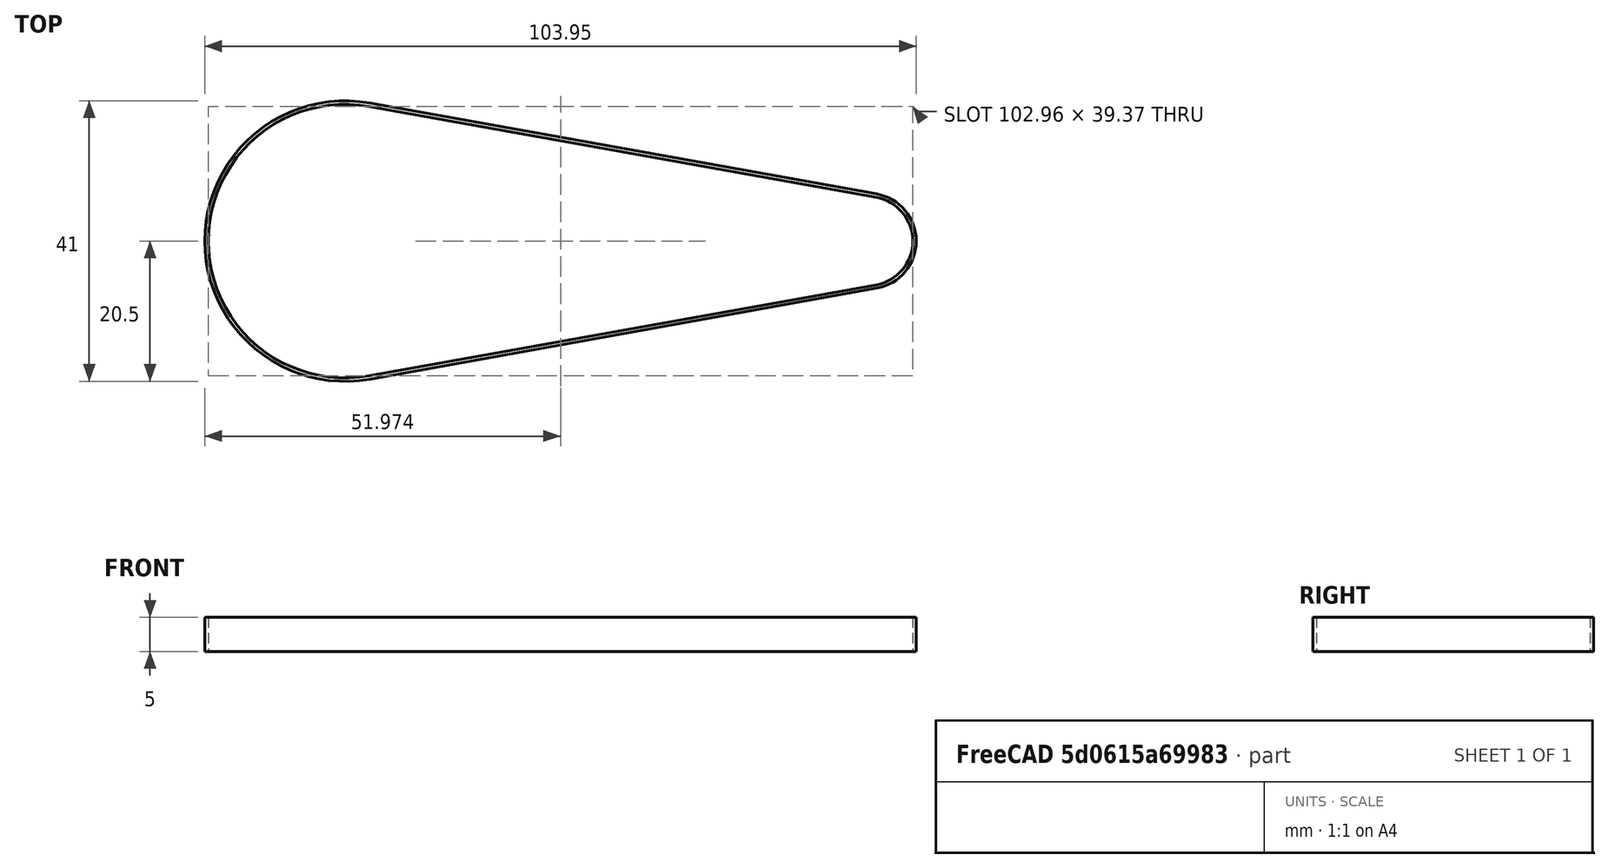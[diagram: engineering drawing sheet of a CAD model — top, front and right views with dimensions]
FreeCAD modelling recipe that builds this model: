
FCSTD DOCUMENT  (FreeCAD 0.20R29177 +426 (Git))
Label: smallerBelt
License: All rights reserved
LicenseURL: http://en.wikipedia.org/wiki/All_rights_reserved
objects: PartDesign::CoordinateSystem×2, Sketcher::SketchObject×1, PartDesign::Pad×1, PartDesign::Body×1
note: 6 computed .brp shape members not serialized (recipe doc carries the construction recipe); baked Part::Feature solids carry a one-line shape summary decoded from their .brp

FEATURE [Sketcher::SketchObject] Sketch
  FullyConstrained = false
  MapMode = 5
  Support = -> [XY_Plane]
  sketch-geometry (8):
    g0: ArcOfCircle CenterX=-48.7141 CenterY=0 CenterZ=0 NormalX=0 NormalY=0 NormalZ=1 AngleXU=0 Radius=20 StartAngle=1.3933 EndAngle=4.88989
    g1: ArcOfCircle CenterX=27.743 CenterY=0 CenterZ=0 NormalX=0 NormalY=0 NormalZ=1 AngleXU=0 Radius=6.5 StartAngle=4.88989 EndAngle=7.67648
    g2: LineSegment StartX=-45.1827 StartY=19.6858 StartZ=0 EndX=28.8907 EndY=6.39787 EndZ=0
    g3: LineSegment StartX=-45.1827 StartY=-19.6858 StartZ=0 EndX=28.8907 EndY=-6.39787 EndZ=0
    g4: ArcOfCircle CenterX=-48.7141 CenterY=0 CenterZ=0 NormalX=0 NormalY=0 NormalZ=1 AngleXU=0 Radius=20.5 StartAngle=1.3933 EndAngle=4.88989
    g5: ArcOfCircle CenterX=27.743 CenterY=0 CenterZ=0 NormalX=0 NormalY=0 NormalZ=1 AngleXU=0 Radius=7 StartAngle=4.88989 EndAngle=7.67648
    g6: LineSegment StartX=-45.0944 StartY=20.1779 StartZ=0 EndX=28.979 EndY=6.89002 EndZ=0
    g7: LineSegment StartX=-45.0944 StartY=-20.1779 StartZ=0 EndX=28.979 EndY=-6.89002 EndZ=0
  constraints (16):
    c: PointOnObject(g0,g-1)
    c: PointOnObject(g1,g-1)
    c: Diameter(g0) = 40
    c: Diameter(g1) = 13
    c: Tangent(g0,g3) = -1.5708
    c: Tangent(g0,g2) = 1.5708
    c: Tangent(g1,g2) = 1.5708
    c: Tangent(g1,g3) = -1.5708
    c: Diameter(g4) = 41
    c: Diameter(g5) = 14
    c: Tangent(g4,g7) = -1.5708
    c: Tangent(g4,g6) = 1.5708
    c: Tangent(g5,g6) = 1.5708
    c: Tangent(g5,g7) = -1.5708
    c: Coincident(g5,g1)
    c: Coincident(g4,g0)
FEATURE [PartDesign::Pad] Pad
  Direction = (0,0,1)
  Length = 5
  Length2 = 10
  Profile = -> Sketch
  ReferenceAxis = -> Sketch [N_Axis]
  Type = 0
FEATURE [PartDesign::CoordinateSystem] LCS_gear60
  AttacherType = Attacher::AttachEngine3D
  MapMode = 11
  Placement = pos=(-48.7141,3.6e-15,0) rot=(0,0,1;2.96409rad)
  Support = -> [Pad]
FEATURE [PartDesign::CoordinateSystem] LCS_gear20
  AttacherType = Attacher::AttachEngine3D
  MapMode = 11
  Placement = pos=(27.743,9e-16,0) rot=(0,0,1;0.1775rad)
  Support = -> [Pad]
FEATURE [PartDesign::Body] Body  label="smallerBelt_Body"
  Group = -> [Sketch,Pad,LCS_gear60,LCS_gear20]
  Origin = -> Origin
  Tip = -> Pad
